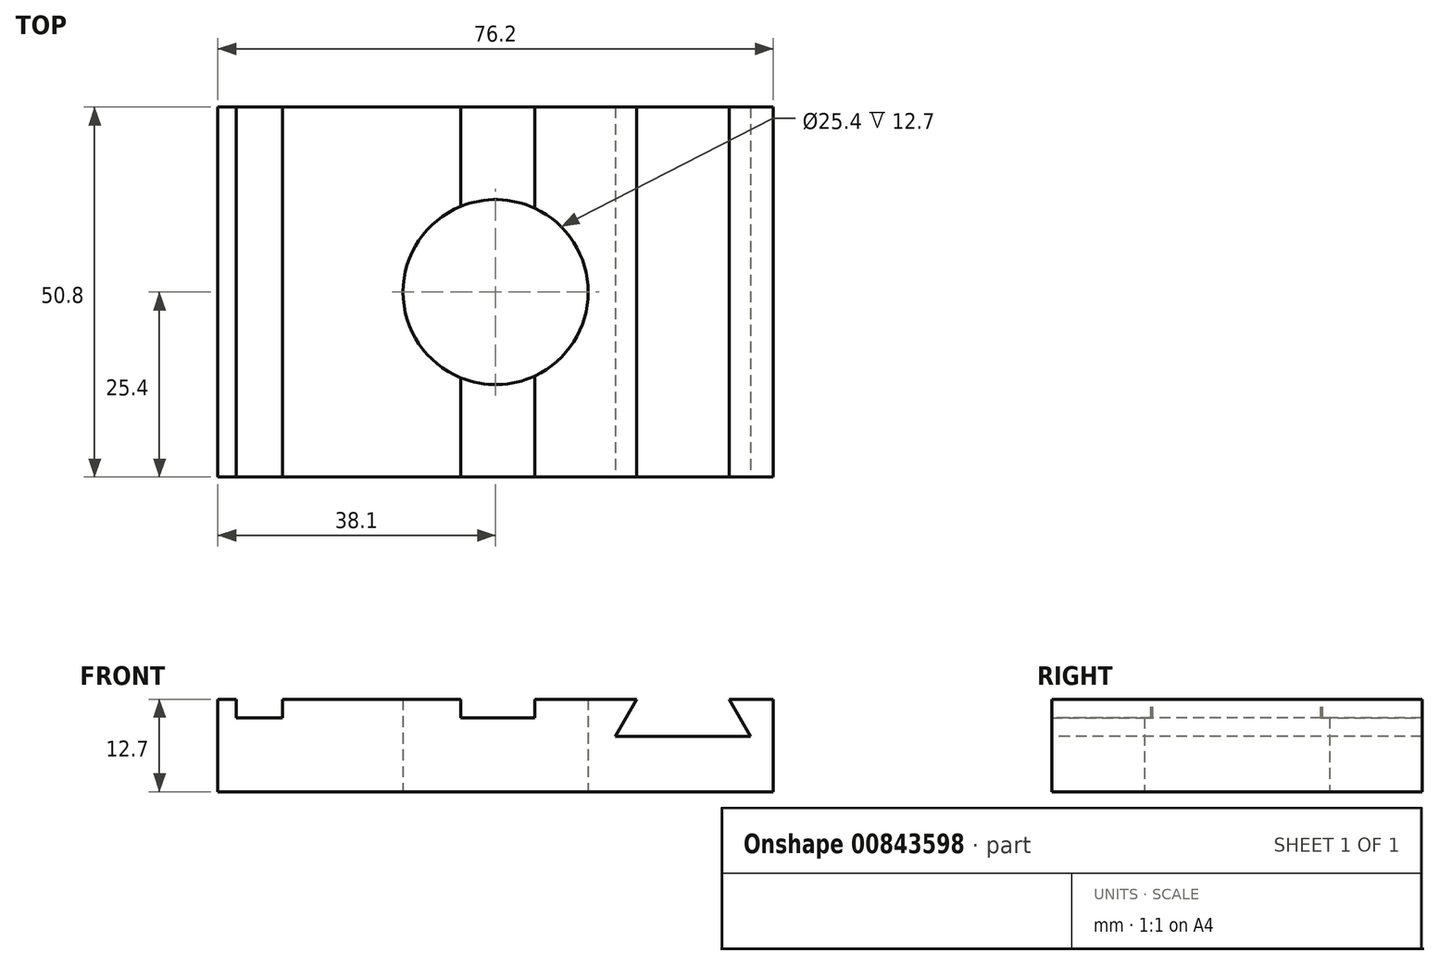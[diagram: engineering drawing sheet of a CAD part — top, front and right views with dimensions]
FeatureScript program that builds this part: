
annotation { "Feature Type Name" : "Feature", "Feature Type Description" : "" }
export const myFeature = defineFeature(function(context is Context, id is Id, definition is map)
    precondition{}
    {
        {
            var Q0;
            Q0=qCreatedBy(makeId("Top.planeOp"),FACE);
            var sketch = newSketch(context, id + "F0", { "sketchPlane" : qUnion([Q0])});
            skLineSegment(sketch, "E0.bottom", {"start": v(38.1, -25.4) * mm, "end": v(-38.1, -25.4) * mm});
            skLineSegment(sketch, "E0.top", {"start": v(38.1, 25.4) * mm, "end": v(-38.1, 25.4) * mm});
            skLineSegment(sketch, "E0.left", {"start": v(38.1, -25.4) * mm, "end": v(38.1, 25.4) * mm});
            skLineSegment(sketch, "E0.right", {"start": v(-38.1, -25.4) * mm, "end": v(-38.1, 25.4) * mm});
            skPoint(sketch, "E0.middle", {"position": v(0, 0) * mm});
            skCircle(sketch, "E1", {"center": v(0, 0) * mm, "radius": 12.7 * mm});
            skSolve(sketch);
        }
        {
            var Q0;
            Q0=makeQuery(id+"F0.imprint","IMPRINT",FACE,{"disambiguationData":[TD([[makeQuery(id+"F0.imprint","IMPRINT",EDGE,{"derivedFrom":sQuery(id+"F0.wireOp",EDGE,"E0.bottom")}),-1.0]])]});
            extrude(context, id + "F1", {"entities" : qUnion([Q0]), "depth" : 12.7 * mm, "offsetDistance" : 25.4 * mm});
        }
        {
            var Q0;
            Q0=makeQuery(id+"F1.opExtrude","CAP_FACE",FACE,{"disambiguationData":[OSD([sQuery(id+"F0.wireOp",EDGE,"E0.bottom"),sQuery(id+"F0.wireOp",EDGE,"E0.top"),sQuery(id+"F0.wireOp",EDGE,"E0.left"),sQuery(id+"F0.wireOp",EDGE,"E0.right"),sQuery(id+"F0.wireOp",EDGE,"E1")])],"isStart":false});
            var sketch = newSketch(context, id + "F2", { "sketchPlane" : qUnion([Q0])});
            skLineSegment(sketch, "E2.bottom", {"start": v(-35.56, 25.4) * mm, "end": v(-29.21, 25.4) * mm});
            skLineSegment(sketch, "E2.top", {"start": v(-35.56, -25.4) * mm, "end": v(-29.21, -25.4) * mm});
            skLineSegment(sketch, "E2.left", {"start": v(-35.56, 25.4) * mm, "end": v(-35.56, -25.4) * mm});
            skLineSegment(sketch, "E2.right", {"start": v(-29.21, 25.4) * mm, "end": v(-29.21, -25.4) * mm});
            skLineSegment(sketch, "E3", {"start": v(-4.79, 25.4) * mm, "end": v(-4.79, -25.4) * mm});
            skLineSegment(sketch, "E4", {"start": v(-4.79, -25.4) * mm, "end": v(5.37, -25.4) * mm});
            skLineSegment(sketch, "E5", {"start": v(5.37, -25.4) * mm, "end": v(5.37, 25.4) * mm});
            skPoint(sketch, "E6", {"position": v(0, 0) * mm});
            skLineSegment(sketch, "E7", {"start": v(0.3, -25.4) * mm, "end": v(0.3, 25.4) * mm, "construction": true});
            skPoint(sketch, "E7.endSnap0", {"position": v(0, 25.4) * mm});
            skSolve(sketch);
        }
        {
            var Q0;
            Q0=makeQuery(id+"F2.imprint","IMPRINT",FACE,{"disambiguationData":[TD([[makeQuery(id+"F2.imprint","IMPRINT",EDGE,{"derivedFrom":sQuery(id+"F2.wireOp",EDGE,"E2.bottom")}),1.0]])]});
            var Q1;
            {var subQ0=sQuery(id+"F2.wireOp",EDGE,"E3");var subQ1=makeQuery(id+"F1.opExtrude","CAP_EDGE",EDGE,{"disambiguationData":[OSD([sQuery(id+"F0.wireOp",EDGE,"E0.top")])],"isStart":false});var subQ2=makeQuery(id+"F2.imprint","INTERSECT",VERTEX,{"derivedFrom":[subQ1,subQ0]});Q1=makeQuery(id+"F2.imprint","IMPRINT",FACE,{"disambiguationData":[TD([[makeQuery(id+"F2.imprint","IMPRINT",EDGE,{"disambiguationData":[TD([[subQ2,-1.0]])],"derivedFrom":subQ0}),1.0]])]});}
            var Q2;
            {var subQ0=sQuery(id+"F2.wireOp",EDGE,"E4");Q2=makeQuery(id+"F2.imprint","IMPRINT",FACE,{"disambiguationData":[TD([[makeQuery(id+"F2.imprint","IMPRINT",EDGE,{"derivedFrom":subQ0}),-1.0]])]});}
            extrude(context, id + "F3", {"entities" : qUnion([Q0, Q1, Q2]), "operationType" : NewBodyOperationType.REMOVE, "oppositeDirection" : true, "depth" : 2.54 * mm, "offsetDistance" : 25.4 * mm});
        }
        {
            var Q0;
            Q0=makeQuery(id+"F1.opExtrude","SWEPT_FACE",FACE,{"disambiguationData":[OSD([sQuery(id+"F0.wireOp",EDGE,"E0.bottom")])]});
            var sketch = newSketch(context, id + "F4", { "sketchPlane" : qUnion([Q0])});
            skLineSegment(sketch, "E8", {"start": v(19.34, 12.7) * mm, "end": v(16.4, 7.62) * mm});
            skLineSegment(sketch, "E9", {"start": v(16.4, 7.62) * mm, "end": v(34.97, 7.62) * mm});
            skLineSegment(sketch, "E10", {"start": v(34.97, 7.62) * mm, "end": v(32.04, 12.7) * mm});
            skPoint(sketch, "E11", {"position": v(25.7, 7.62) * mm});
            skLineSegment(sketch, "E12", {"start": v(25.7, 7.62) * mm, "end": v(25.7, 12.7) * mm, "construction": true});
            skSolve(sketch);
        }
        {
            var Q0;
            {var subQ0=sQuery(id+"F4.wireOp",EDGE,"E8");Q0=makeQuery(id+"F4.imprint","IMPRINT",FACE,{"disambiguationData":[TD([[makeQuery(id+"F4.imprint","IMPRINT",EDGE,{"derivedFrom":subQ0}),1.0]])]});}
            extrude(context, id + "F5", {"entities" : qUnion([Q0]), "operationType" : NewBodyOperationType.REMOVE, "endBound" : BoundingType.THROUGH_ALL, "oppositeDirection" : true, "depth" : 25.4 * mm, "offsetDistance" : 25.4 * mm});
        }
    });
